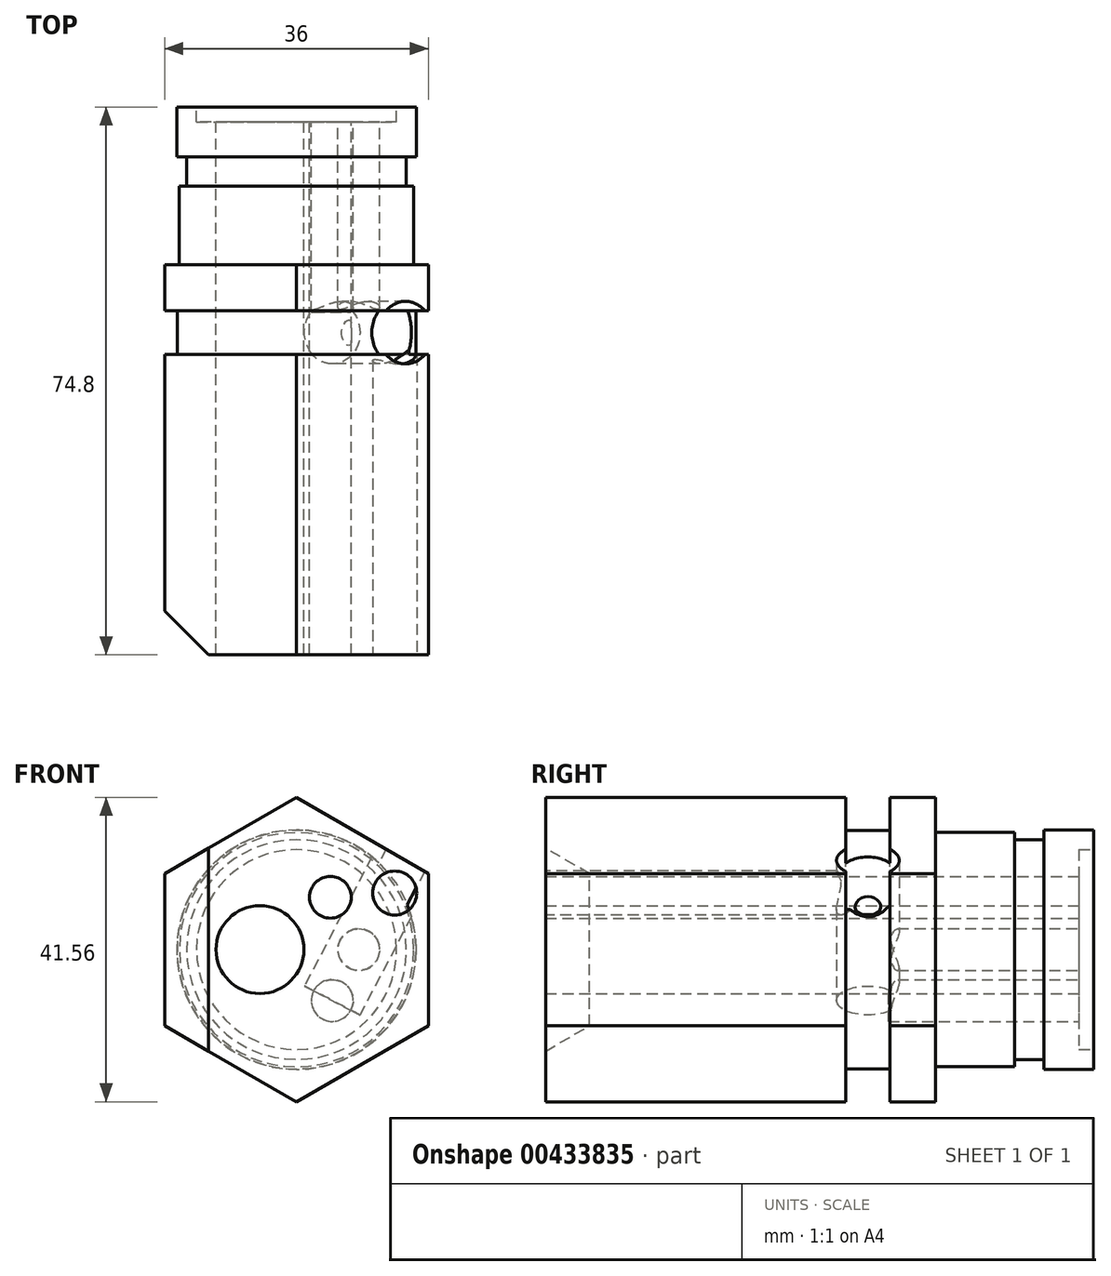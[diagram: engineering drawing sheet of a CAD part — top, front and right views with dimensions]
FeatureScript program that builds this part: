
annotation { "Feature Type Name" : "Feature", "Feature Type Description" : "" }
export const myFeature = defineFeature(function(context is Context, id is Id, definition is map)
    precondition{}
    {
        {
            var Q0;
            Q0=qCreatedBy(makeId("Front.planeOp"),FACE);
            var sketch = newSketch(context, id + "F0", { "sketchPlane" : qUnion([Q0])});
            skCircle(sketch, "E0.cCircle", {"center": v(0, 0) * mm, "radius": 18 * mm, "construction": true});
            skLineSegment(sketch, "E0.0", {"start": v(18, -10.4) * mm, "end": v(0, -20.78) * mm});
            skLineSegment(sketch, "E0.1", {"start": v(0, -20.78) * mm, "end": v(-18, -10.4) * mm});
            skLineSegment(sketch, "E0.2", {"start": v(-18, -10.4) * mm, "end": v(-18, 10.4) * mm});
            skLineSegment(sketch, "E0.3", {"start": v(-18, 10.4) * mm, "end": v(0, 20.78) * mm});
            skLineSegment(sketch, "E0.4", {"start": v(0, 20.78) * mm, "end": v(18, 10.4) * mm});
            skLineSegment(sketch, "E0.5", {"start": v(18, 10.4) * mm, "end": v(18, -10.4) * mm});
            skPoint(sketch, "E0.0.midPoint", {"position": v(9, -15.59) * mm});
            skSolve(sketch);
        }
        {
            var Q0;
            Q0 = qSketchRegion(id + "F0", true);
            extrude(context, id + "F1", {"entities" : qUnion([Q0]), "oppositeDirection" : true, "depth" : 41 * mm});
        }
        {
            var Q0;
            Q0=makeQuery(id+"F1.opExtrude","CAP_FACE",FACE,{"disambiguationData":[OSD([sQuery(id+"F0.wireOp",EDGE,"E0.0"),sQuery(id+"F0.wireOp",EDGE,"E0.1"),sQuery(id+"F0.wireOp",EDGE,"E0.2"),sQuery(id+"F0.wireOp",EDGE,"E0.3"),sQuery(id+"F0.wireOp",EDGE,"E0.4"),sQuery(id+"F0.wireOp",EDGE,"E0.5")])],"isStart":false});
            var sketch = newSketch(context, id + "F2", { "sketchPlane" : qUnion([Q0])});
            skCircle(sketch, "E1", {"center": v(0, 0) * mm, "radius": 16.3 * mm});
            skSolve(sketch);
        }
        {
            var Q0;
            Q0 = qSketchRegion(id + "F2", true);
            extrude(context, id + "F3", {"entities" : qUnion([Q0]), "operationType" : NewBodyOperationType.ADD, "depth" : 6 * mm});
        }
        {
            var Q0;
            Q0=makeQuery(id+"F3.opExtrude","CAP_FACE",FACE,{"disambiguationData":[OSD([sQuery(id+"F2.wireOp",EDGE,"E1")])],"isStart":false});
            var sketch = newSketch(context, id + "F4", { "sketchPlane" : qUnion([Q0])});
            skCircle(sketch, "E2.cCircle", {"center": v(0, 0) * mm, "radius": 18 * mm, "construction": true});
            skLineSegment(sketch, "E2.0", {"start": v(18, -10.4) * mm, "end": v(0, -20.78) * mm});
            skLineSegment(sketch, "E2.1", {"start": v(0, -20.78) * mm, "end": v(-18, -10.4) * mm});
            skLineSegment(sketch, "E2.2", {"start": v(-18, -10.4) * mm, "end": v(-18, 10.4) * mm});
            skLineSegment(sketch, "E2.3", {"start": v(-18, 10.4) * mm, "end": v(0, 20.78) * mm});
            skLineSegment(sketch, "E2.4", {"start": v(0, 20.78) * mm, "end": v(18, 10.4) * mm});
            skLineSegment(sketch, "E2.5", {"start": v(18, 10.4) * mm, "end": v(18, -10.4) * mm});
            skPoint(sketch, "E2.0.midPoint", {"position": v(9, -15.59) * mm});
            skSolve(sketch);
        }
        {
            var Q0;
            Q0 = qSketchRegion(id + "F4", true);
            extrude(context, id + "F5", {"entities" : qUnion([Q0]), "operationType" : NewBodyOperationType.ADD, "depth" : 6.25 * mm});
        }
        {
            var Q0;
            Q0=makeQuery(id+"F5.opExtrude","CAP_FACE",FACE,{"disambiguationData":[OSD([sQuery(id+"F4.wireOp",EDGE,"E2.0"),sQuery(id+"F4.wireOp",EDGE,"E2.1"),sQuery(id+"F4.wireOp",EDGE,"E2.2"),sQuery(id+"F4.wireOp",EDGE,"E2.3"),sQuery(id+"F4.wireOp",EDGE,"E2.4"),sQuery(id+"F4.wireOp",EDGE,"E2.5")])],"isStart":false});
            var sketch = newSketch(context, id + "F6", { "sketchPlane" : qUnion([Q0])});
            skCircle(sketch, "E3", {"center": v(0, 0) * mm, "radius": 16 * mm});
            skSolve(sketch);
        }
        {
            var Q0;
            Q0=makeQuery(id+"F6.imprint","IMPRINT",FACE,{"disambiguationData":[TD([[makeQuery(id+"F6.imprint","IMPRINT",EDGE,{"derivedFrom":sQuery(id+"F6.wireOp",EDGE,"E3")}),1.0]])]});
            extrude(context, id + "F7", {"entities" : qUnion([Q0]), "operationType" : NewBodyOperationType.ADD, "depth" : 10.75 * mm});
        }
        {
            var Q0;
            Q0=makeQuery(id+"F7.opExtrude","CAP_FACE",FACE,{"disambiguationData":[OSD([sQuery(id+"F6.wireOp",EDGE,"E3")])],"isStart":false});
            var sketch = newSketch(context, id + "F8", { "sketchPlane" : qUnion([Q0])});
            skCircle(sketch, "E4", {"center": v(0, 0) * mm, "radius": 15 * mm});
            skSolve(sketch);
        }
        {
            var Q0;
            Q0 = qSketchRegion(id + "F8", true);
            extrude(context, id + "F9", {"entities" : qUnion([Q0]), "operationType" : NewBodyOperationType.ADD, "depth" : 4 * mm});
        }
        {
            var Q0;
            Q0=makeQuery(id+"F9.opExtrude","CAP_FACE",FACE,{"disambiguationData":[OSD([sQuery(id+"F8.wireOp",EDGE,"E4")])],"isStart":false});
            var sketch = newSketch(context, id + "F10", { "sketchPlane" : qUnion([Q0])});
            skCircle(sketch, "E5", {"center": v(0, 0) * mm, "radius": 16.35 * mm});
            skSolve(sketch);
        }
        {
            var Q0;
            Q0 = qSketchRegion(id + "F10", true);
            extrude(context, id + "F11", {"entities" : qUnion([Q0]), "operationType" : NewBodyOperationType.ADD, "depth" : 6.8 * mm});
        }
        {
            var Q0;
            Q0=makeQuery(id+"F11.opExtrude","CAP_FACE",FACE,{"disambiguationData":[OSD([sQuery(id+"F10.wireOp",EDGE,"E5")])],"isStart":false});
            var sketch = newSketch(context, id + "F12", { "sketchPlane" : qUnion([Q0])});
            skCircle(sketch, "E6", {"center": v(0, 0) * mm, "radius": 13.65 * mm});
            skSolve(sketch);
        }
        {
            var Q0;
            Q0 = qSketchRegion(id + "F12", true);
            extrude(context, id + "F13", {"entities" : qUnion([Q0]), "operationType" : NewBodyOperationType.REMOVE, "oppositeDirection" : true, "depth" : 2 * mm});
        }
        {
            var Q0;
            Q0=makeQuery(id+"F13.boolean.opBoolean","COPY",FACE,{"derivedFrom":makeQuery(id+"F13.opExtrude","CAP_FACE",FACE,{"disambiguationData":[OSD([sQuery(id+"F12.wireOp",EDGE,"E6")])],"isStart":false})});
            var sketch = newSketch(context, id + "F14", { "sketchPlane" : qUnion([Q0])});
            skCircle(sketch, "E7", {"center": v(5, 0) * mm, "radius": 6 * mm});
            skSolve(sketch);
        }
        {
            var Q0;
            Q0 = qSketchRegion(id + "F14", true);
            extrude(context, id + "F15", {"entities" : qUnion([Q0]), "operationType" : NewBodyOperationType.REMOVE, "endBound" : BoundingType.THROUGH_ALL, "oppositeDirection" : true, "depth" : 25 * mm});
        }
        {
            var Q0;
            Q0=makeQuery(id+"F13.boolean.opBoolean","COPY",FACE,{"derivedFrom":makeQuery(id+"F13.opExtrude","CAP_FACE",FACE,{"disambiguationData":[OSD([sQuery(id+"F12.wireOp",EDGE,"E6")])],"isStart":false})});
            var sketch = newSketch(context, id + "F16", { "sketchPlane" : qUnion([Q0])});
            skCircle(sketch, "E8", {"center": v(-4.87, -6.95) * mm, "radius": 2.85 * mm});
            skCircle(sketch, "E9", {"center": v(-8.5, 0) * mm, "radius": 2.85 * mm});
            skCircle(sketch, "E10", {"center": v(-4.62, 7.15) * mm, "radius": 3 * mm});
            skSolve(sketch);
        }
        {
            var Q0;
            Q0=makeQuery(id+"F16.imprint","IMPRINT",FACE,{"disambiguationData":[TD([[makeQuery(id+"F16.imprint","IMPRINT",EDGE,{"derivedFrom":sQuery(id+"F16.wireOp",EDGE,"E8")}),1.0]])]});
            var Q1;
            Q1=makeQuery(id+"F16.imprint","IMPRINT",FACE,{"disambiguationData":[TD([[makeQuery(id+"F16.imprint","IMPRINT",EDGE,{"derivedFrom":sQuery(id+"F16.wireOp",EDGE,"E9")}),1.0]])]});
            extrude(context, id + "F17", {"entities" : qUnion([Q0, Q1]), "operationType" : NewBodyOperationType.REMOVE, "oppositeDirection" : true, "depth" : 26 * mm});
        }
        {
            var Q0;
            Q0=qCreatedBy(makeId("Front.planeOp"),FACE);
            cPlane(context, id + "F18", {"entities" : qUnion([Q0]), "cplaneType" : CPlaneType.OFFSET, "offset" : 44 * mm, "oppositeDirection" : true, "width" : 150 * mm, "height" : 150 * mm});
        }
        {
            var Q0;
            Q0=qCreatedBy(id+"F18.planeOp",FACE);
            var sketch = newSketch(context, id + "F19", { "sketchPlane" : qUnion([Q0])});
            skLineSegment(sketch, "E11", {"start": v(4.87, -6.95) * mm, "end": v(18.5, 19.15) * mm, "construction": true});
            skCircle(sketch, "E12.0", {"center": v(8.5, 0) * mm, "radius": 2.85 * mm, "construction": true});
            skLineSegment(sketch, "E13", {"start": v(15.22, 12.87) * mm, "end": v(19.01, 10.89) * mm});
            skLineSegment(sketch, "E14", {"start": v(19.01, 10.89) * mm, "end": v(8.66, -8.93) * mm});
            skLineSegment(sketch, "E15", {"start": v(8.66, -8.93) * mm, "end": v(4.87, -6.95) * mm});
            skLineSegment(sketch, "E16", {"start": v(15.22, 12.87) * mm, "end": v(4.87, -6.95) * mm});
            skSolve(sketch);
        }
        {
            var Q0;
            Q0 = qSketchRegion(id + "F19", true);
            var Q1;
            Q1=sQuery(id+"F19.wireOp",EDGE,"E11");
            revolve(context, id + "F20", {"operationType" : NewBodyOperationType.REMOVE, "entities" : qUnion([Q0]), "axis" : qUnion([Q1]), "revolveType" : RevolveType.FULL});
        }
        {
            var Q0;
            Q0=makeQuery(id+"F1.opExtrude","CAP_FACE",FACE,{"disambiguationData":[OSD([sQuery(id+"F0.wireOp",EDGE,"E0.0"),sQuery(id+"F0.wireOp",EDGE,"E0.1"),sQuery(id+"F0.wireOp",EDGE,"E0.2"),sQuery(id+"F0.wireOp",EDGE,"E0.3"),sQuery(id+"F0.wireOp",EDGE,"E0.4"),sQuery(id+"F0.wireOp",EDGE,"E0.5")])],"isStart":true});
            var sketch = newSketch(context, id + "F21", { "sketchPlane" : qUnion([Q0])});
            skCircle(sketch, "E17", {"center": v(13.4, 7.74) * mm, "radius": 3 * mm});
            skSolve(sketch);
        }
        {
            var Q0;
            Q0 = qSketchRegion(id + "F21", true);
            extrude(context, id + "F22", {"entities" : qUnion([Q0]), "operationType" : NewBodyOperationType.REMOVE, "oppositeDirection" : true, "depth" : 45 * mm});
        }
        {
            var Q0;
            Q0=makeQuery(id+"F1.opExtrude","CAP_EDGE",EDGE,{"disambiguationData":[OSD([sQuery(id+"F0.wireOp",EDGE,"E0.2")])],"isStart":true});
            chamfer(context, id + "F23", {"entities" : qUnion([Q0]), "width" : 6 * mm, "tangentPropagation" : true});
        }
        {
            var Q0;
            Q0=makeQuery(id+"F13.boolean.opBoolean","COPY",FACE,{"derivedFrom":makeQuery(id+"F13.opExtrude","CAP_FACE",FACE,{"disambiguationData":[OSD([sQuery(id+"F12.wireOp",EDGE,"E6")])],"isStart":false})});
            var sketch = newSketch(context, id + "F24", { "sketchPlane" : qUnion([Q0])});
            skCircle(sketch, "E18", {"center": v(-4.62, 7.15) * mm, "radius": 2.85 * mm});
            skPoint(sketch, "E19", {"position": v(-8.5, 0) * mm});
            skSolve(sketch);
        }
        {
            var Q0;
            Q0 = qSketchRegion(id + "F24", true);
            extrude(context, id + "F25", {"entities" : qUnion([Q0]), "operationType" : NewBodyOperationType.REMOVE, "endBound" : BoundingType.THROUGH_ALL, "oppositeDirection" : true, "depth" : 25 * mm});
        }
    });
